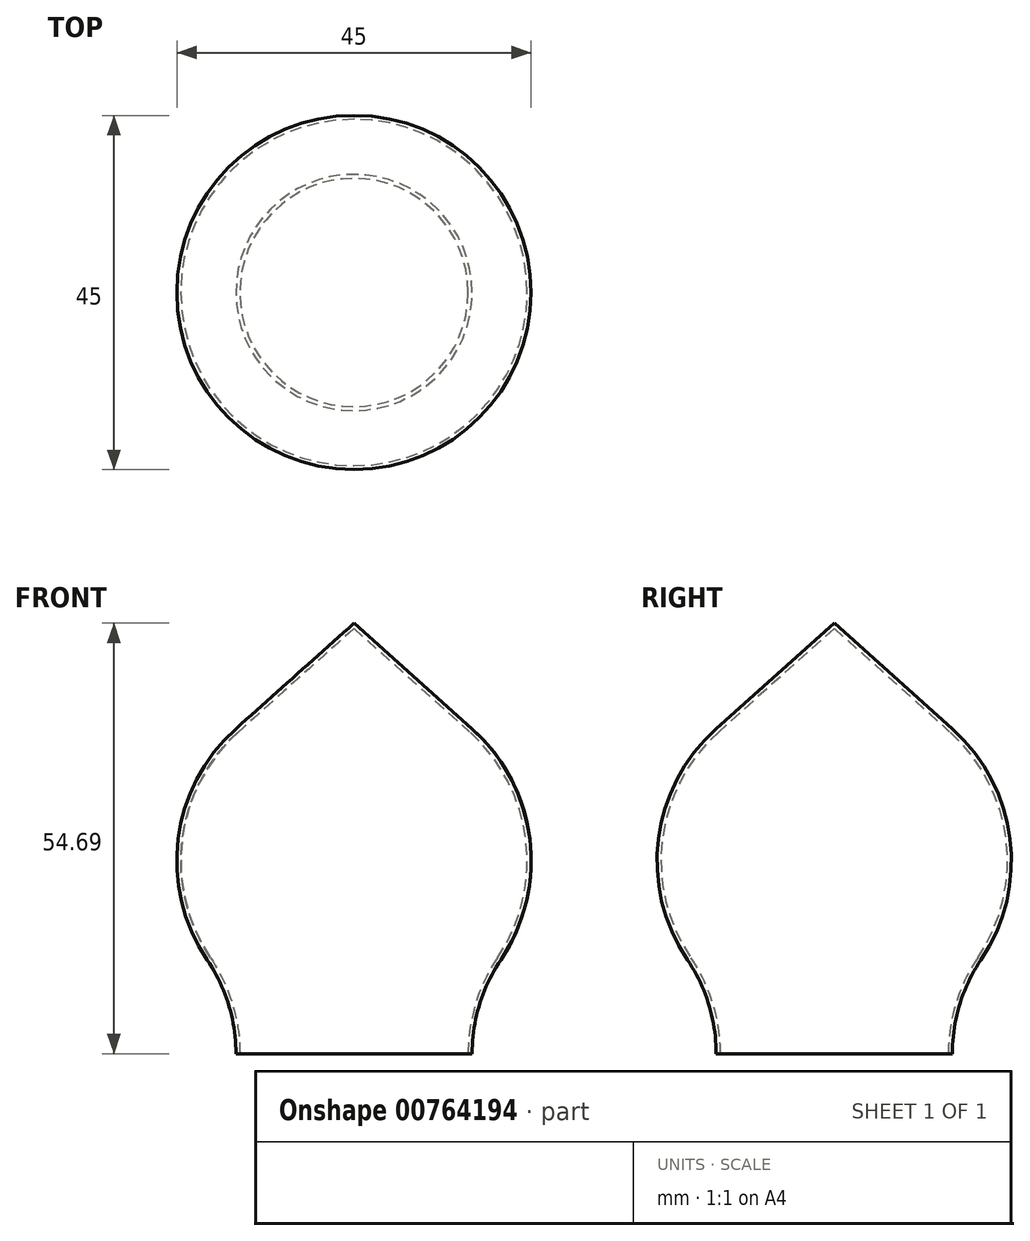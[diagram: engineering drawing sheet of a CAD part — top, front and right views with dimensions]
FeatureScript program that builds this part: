
annotation { "Feature Type Name" : "Feature", "Feature Type Description" : "" }
export const myFeature = defineFeature(function(context is Context, id is Id, definition is map)
    precondition{}
    {
        {
            var Q0;
            Q0=qCreatedBy(makeId("Front.planeOp"),FACE);
            var sketch = newSketch(context, id + "F0", { "sketchPlane" : qUnion([Q0])});
            skArc(sketch, "E0", {"start": v(-15, 16.77) * mm, "mid": v(-22.33, 2.77) * mm, "end": v(-18.64, -12.6) * mm});
            skArc(sketch, "E1", {"start": v(-15, -24.5) * mm, "mid": v(-15.93, -18.27) * mm, "end": v(-18.64, -12.6) * mm});
            skLineSegment(sketch, "E2", {"start": v(0, 36.3) * mm, "end": v(0, -65.15) * mm});
            skLineSegment(sketch, "E3", {"start": v(-44.88, -24.5) * mm, "end": v(26.54, -24.5) * mm});
            skPoint(sketch, "E4", {"position": v(-15, -24.5) * mm});
            skPoint(sketch, "E5", {"position": v(0, 22.5) * mm});
            skPoint(sketch, "E6", {"position": v(-7.5, -24.5) * mm});
            skPoint(sketch, "E7", {"position": v(-15, 16.77) * mm});
            skLineSegment(sketch, "E8", {"start": v(-15, 16.77) * mm, "end": v(0, 30.19) * mm});
            skSolve(sketch);
        }
        {
            var Q0;
            {var subQ0=sQuery(id+"F0.wireOp",EDGE,"E0");Q0=makeQuery(id+"F0.imprint","IMPRINT",FACE,{"disambiguationData":[TD([[makeQuery(id+"F0.imprint","IMPRINT",EDGE,{"derivedFrom":subQ0}),1.0]])]});}
            var Q1;
            Q1=sQuery(id+"F0.wireOp",EDGE,"E2");
            revolve(context, id + "F1", {"surfaceOperationType" : NewSurfaceOperationType.NEW, "entities" : qUnion([Q0]), "axis" : qUnion([Q1]), "revolveType" : RevolveType.FULL});
        }
        {
            var Q0;
            Q0=makeQuery(id+"F1.opRevolve","SWEPT_FACE",FACE,{"disambiguationData":[OSD([sQuery(id+"F0.wireOp",EDGE,"E3")])]});
            shell(context, id + "F2", {"entities" : qUnion([Q0]), "thickness" : 0.5 * mm});
        }
    });
